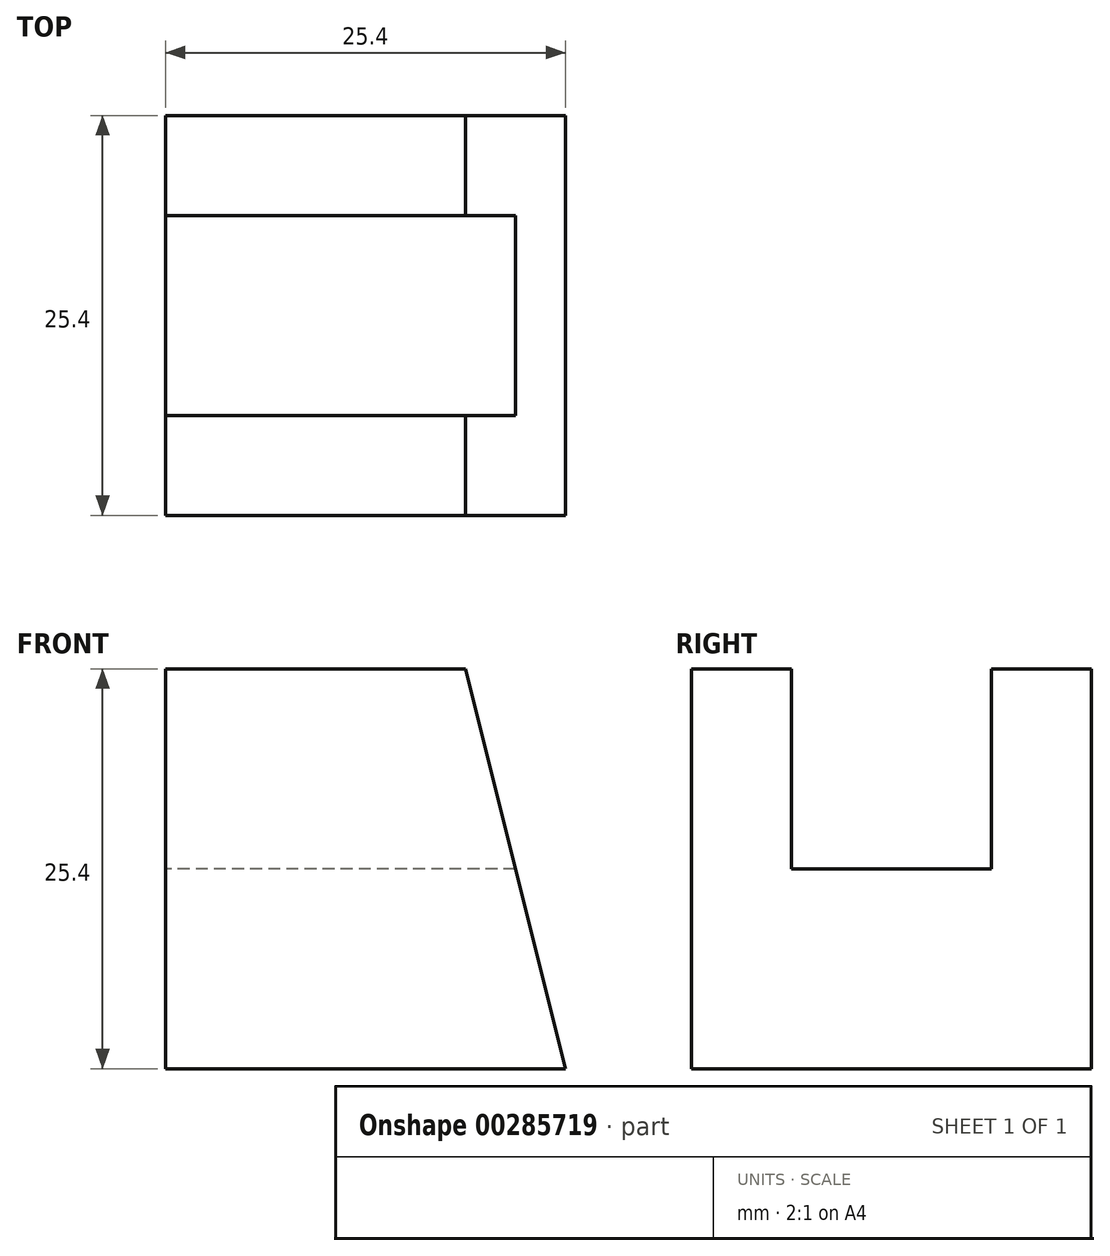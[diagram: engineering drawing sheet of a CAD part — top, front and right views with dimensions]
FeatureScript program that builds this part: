
annotation { "Feature Type Name" : "Feature", "Feature Type Description" : "" }
export const myFeature = defineFeature(function(context is Context, id is Id, definition is map)
    precondition{}
    {
        {
            var Q0;
            Q0=qCreatedBy(makeId("Right.planeOp"),FACE);
            var sketch = newSketch(context, id + "F0", { "sketchPlane" : qUnion([Q0])});
            skLineSegment(sketch, "E0", {"start": v(0, 0) * mm, "end": v(0, 25.4) * mm});
            skLineSegment(sketch, "E1", {"start": v(0, 25.4) * mm, "end": v(6.35, 25.4) * mm});
            skLineSegment(sketch, "E2", {"start": v(6.35, 25.4) * mm, "end": v(6.35, 12.7) * mm});
            skLineSegment(sketch, "E3", {"start": v(6.35, 12.7) * mm, "end": v(19.05, 12.7) * mm});
            skLineSegment(sketch, "E4", {"start": v(19.05, 12.7) * mm, "end": v(19.05, 25.4) * mm});
            skLineSegment(sketch, "E5", {"start": v(19.05, 25.4) * mm, "end": v(25.4, 25.4) * mm});
            skLineSegment(sketch, "E6", {"start": v(25.4, 25.4) * mm, "end": v(25.4, 0) * mm});
            skLineSegment(sketch, "E7", {"start": v(25.4, 0) * mm, "end": v(0, 0) * mm});
            skSolve(sketch);
        }
        {
            var Q0;
            Q0=makeQuery(id+"F0.imprint","IMPRINT",FACE,{"disambiguationData":[TD([[makeQuery(id+"F0.imprint","IMPRINT",EDGE,{"derivedFrom":sQuery(id+"F0.wireOp",EDGE,"E0")}),-1.0]])]});
            extrude(context, id + "F1", {"entities" : qUnion([Q0]), "depth" : 25.4 * mm});
        }
        {
            var Q0;
            Q0=makeQuery(id+"F1.opExtrude","SWEPT_FACE",FACE,{"disambiguationData":[OSD([sQuery(id+"F0.wireOp",EDGE,"E0")])]});
            var sketch = newSketch(context, id + "F2", { "sketchPlane" : qUnion([Q0])});
            skLineSegment(sketch, "E8", {"start": v(0, 25.4) * mm, "end": v(0, 0) * mm});
            skLineSegment(sketch, "E9", {"start": v(0, 0) * mm, "end": v(25.4, 0) * mm});
            skLineSegment(sketch, "E10", {"start": v(0, 25.4) * mm, "end": v(19.05, 25.4) * mm});
            skLineSegment(sketch, "E11", {"start": v(19.05, 25.4) * mm, "end": v(25.4, 0) * mm});
            skSolve(sketch);
        }
        {
            var Q0;
            {var subQ0=sQuery(id+"F2.wireOp",EDGE,"E11");Q0=makeQuery(id+"F2.imprint","IMPRINT",FACE,{"disambiguationData":[TD([[makeQuery(id+"F2.imprint","IMPRINT",EDGE,{"derivedFrom":subQ0}),1.0]])]});}
            extrude(context, id + "F3", {"entities" : qUnion([Q0]), "operationType" : NewBodyOperationType.REMOVE, "oppositeDirection" : true, "depth" : 25.4 * mm});
        }
    });
